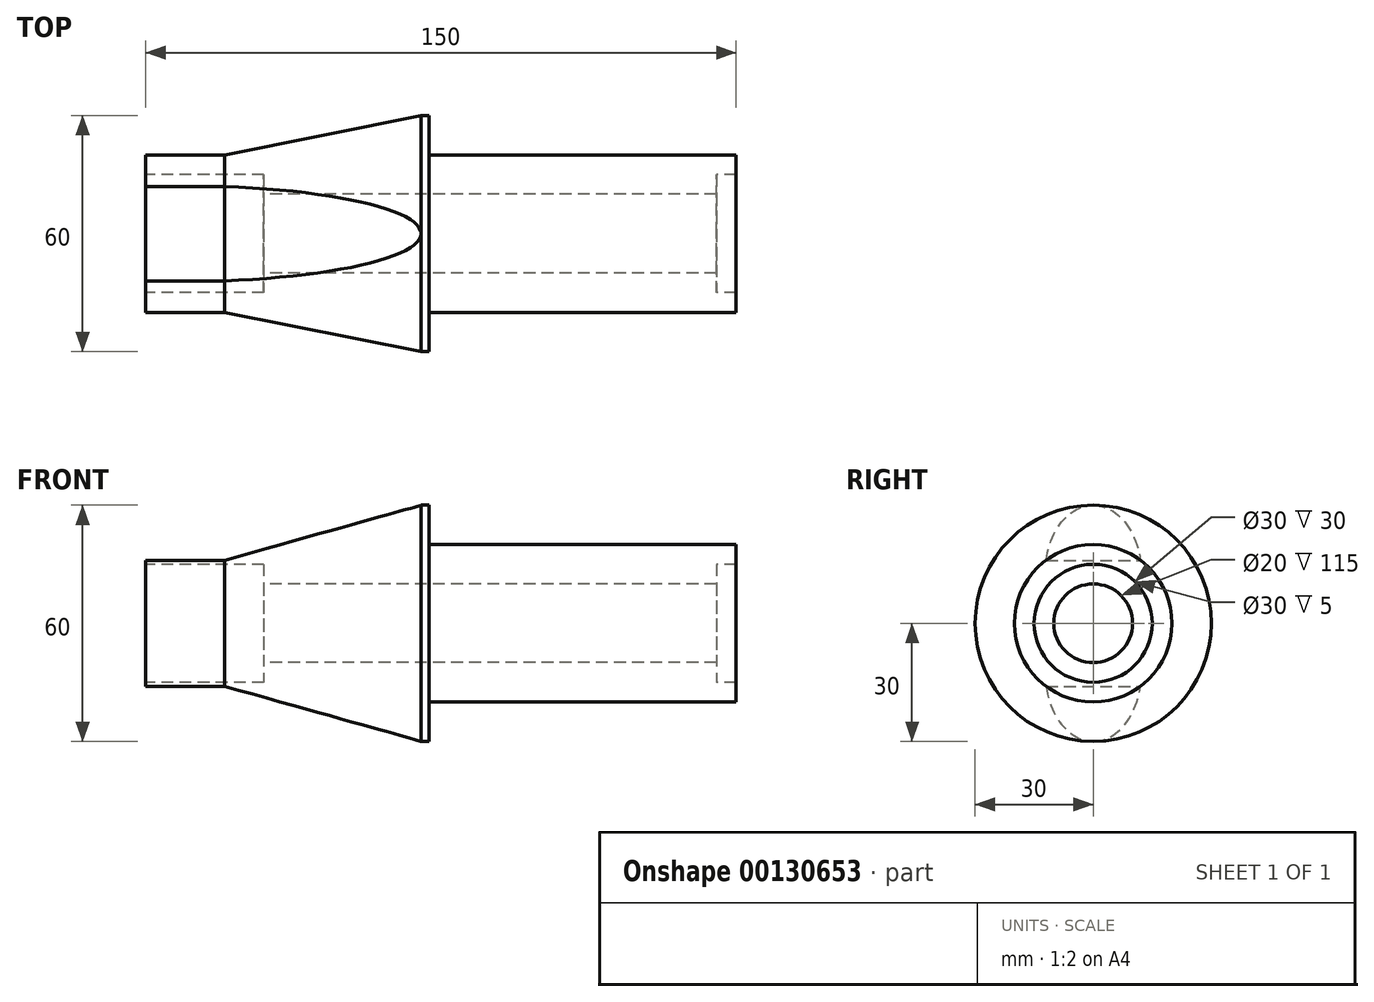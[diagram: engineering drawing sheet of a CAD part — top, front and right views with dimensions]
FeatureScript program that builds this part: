
annotation { "Feature Type Name" : "Feature", "Feature Type Description" : "" }
export const myFeature = defineFeature(function(context is Context, id is Id, definition is map)
    precondition{}
    {
        {
            var Q0;
            Q0=qCreatedBy(makeId("Front.planeOp"),FACE);
            var sketch = newSketch(context, id + "F0", { "sketchPlane" : qUnion([Q0])});
            skLineSegment(sketch, "E0", {"start": v(-51, 15) * mm, "end": v(-21, 15) * mm});
            skLineSegment(sketch, "E1", {"start": v(-21, 15) * mm, "end": v(-21, 10) * mm});
            skLineSegment(sketch, "E2", {"start": v(19, 30) * mm, "end": v(-31, 20) * mm});
            skLineSegment(sketch, "E3", {"start": v(-31, 20) * mm, "end": v(-51, 20) * mm});
            skLineSegment(sketch, "E4", {"start": v(-51, 20) * mm, "end": v(-51, 15) * mm});
            skLineSegment(sketch, "E5", {"start": v(-121.58, 0) * mm, "end": v(180.57, 0) * mm, "construction": true});
            skLineSegment(sketch, "E6", {"start": v(94, 10) * mm, "end": v(94, 15) * mm});
            skLineSegment(sketch, "E7", {"start": v(94, 15) * mm, "end": v(99, 15) * mm});
            skLineSegment(sketch, "E8", {"start": v(99, 20) * mm, "end": v(99, 15) * mm});
            skLineSegment(sketch, "E9", {"start": v(-21, 10) * mm, "end": v(94, 10) * mm});
            skLineSegment(sketch, "E10", {"start": v(19, 30) * mm, "end": v(21, 30) * mm});
            skLineSegment(sketch, "E11", {"start": v(21, 30) * mm, "end": v(21, 20) * mm});
            skLineSegment(sketch, "E12", {"start": v(21, 20) * mm, "end": v(99, 20) * mm});
            skSolve(sketch);
        }
        {
            var Q0;
            Q0 = qSketchRegion(id + "F0", true);
            var Q1;
            Q1=sQuery(id+"F0.wireOp",EDGE,"E5");
            revolve(context, id + "F1", {"entities" : qUnion([Q0]), "axis" : qUnion([Q1]), "revolveType" : RevolveType.FULL});
        }
        {
            var Q0;
            Q0=qCreatedBy(makeId("Front.planeOp"),FACE);
            var sketch = newSketch(context, id + "F2", { "sketchPlane" : qUnion([Q0])});
            skLineSegment(sketch, "E13", {"start": v(-31, 16) * mm, "end": v(19, 30) * mm});
            skLineSegment(sketch, "E14", {"start": v(-31, 19.93) * mm, "end": v(19, 30) * mm});
            skLineSegment(sketch, "E15", {"start": v(-51, 20) * mm, "end": v(-31, 20) * mm});
            skLineSegment(sketch, "E16", {"start": v(-31, 20) * mm, "end": v(19, 30) * mm});
            skLineSegment(sketch, "E17", {"start": v(-51, 20) * mm, "end": v(-51, 16) * mm});
            skLineSegment(sketch, "E18", {"start": v(-51, 16) * mm, "end": v(-31, 16) * mm});
            skLineSegment(sketch, "E19.MirrorCS", {"start": v(-51, -20) * mm, "end": v(-31, -20) * mm});
            skLineSegment(sketch, "E20.MirrorCS", {"start": v(-51, -16) * mm, "end": v(-31, -16) * mm});
            skLineSegment(sketch, "E21.MirrorCS", {"start": v(-51, -20) * mm, "end": v(-51, -16) * mm});
            skLineSegment(sketch, "E22.MirrorCS", {"start": v(-31, -16) * mm, "end": v(19, -30) * mm});
            skLineSegment(sketch, "E23.MirrorCS", {"start": v(-31, -20) * mm, "end": v(19, -30) * mm});
            skSolve(sketch);
        }
        {
            var Q0;
            Q0 = qSketchRegion(id + "F2", true);
            extrude(context, id + "F3", {"entities" : qUnion([Q0]), "operationType" : NewBodyOperationType.REMOVE, "endBound" : BoundingType.SYMMETRIC, "depth" : 60 * mm});
        }
    });
